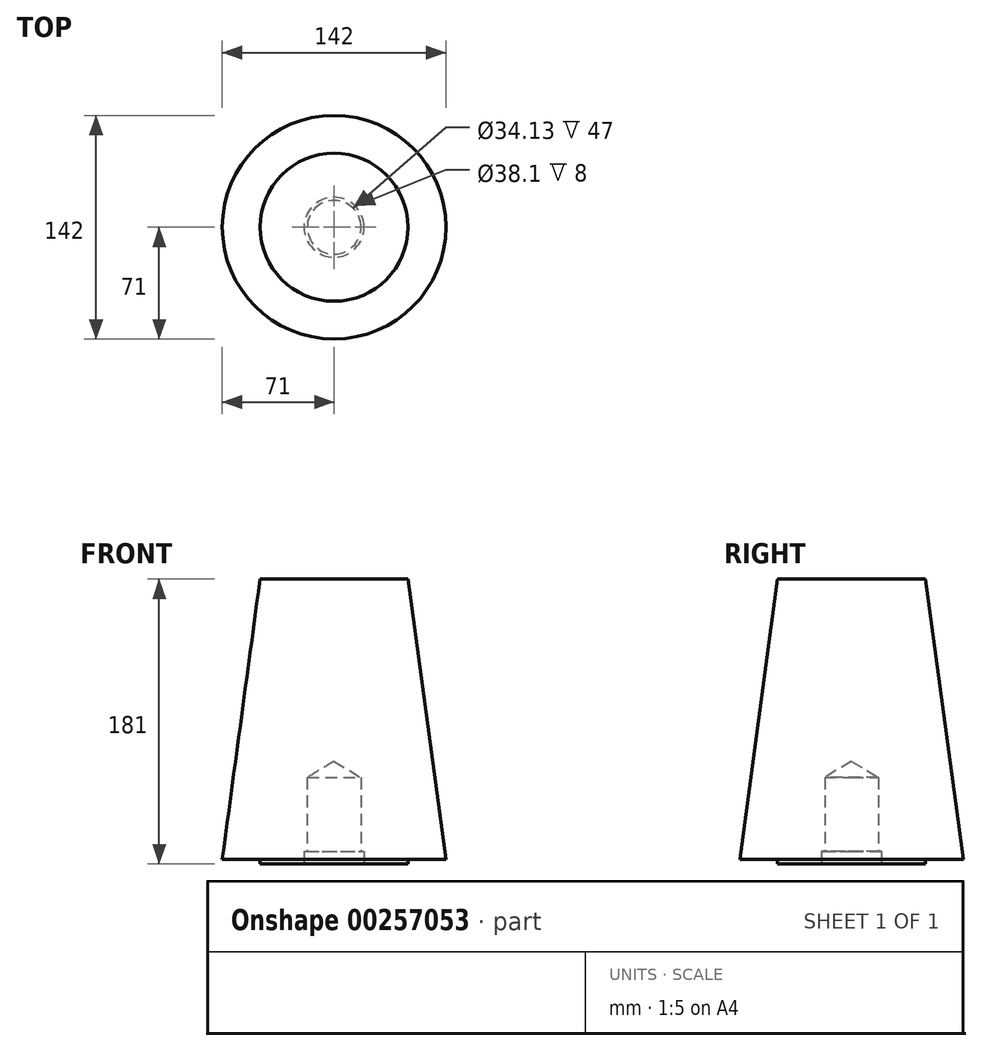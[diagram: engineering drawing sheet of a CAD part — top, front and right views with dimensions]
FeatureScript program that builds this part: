
annotation { "Feature Type Name" : "Feature", "Feature Type Description" : "" }
export const myFeature = defineFeature(function(context is Context, id is Id, definition is map)
    precondition{}
    {
        {
            var Q0;
            Q0=qCreatedBy(makeId("Front.planeOp"),FACE);
            var sketch = newSketch(context, id + "F0", { "sketchPlane" : qUnion([Q0])});
            skLineSegment(sketch, "E0", {"start": v(47, 0) * mm, "end": v(71, 0) * mm});
            skLineSegment(sketch, "E1", {"start": v(0, 0) * mm, "end": v(0, 178) * mm});
            skLineSegment(sketch, "E2", {"start": v(0, 178) * mm, "end": v(47, 178) * mm});
            skLineSegment(sketch, "E3", {"start": v(47, 178) * mm, "end": v(71, 0) * mm});
            skLineSegment(sketch, "E4", {"start": v(0, 0) * mm, "end": v(0, -3) * mm});
            skLineSegment(sketch, "E5", {"start": v(0, -3) * mm, "end": v(47, -3) * mm});
            skLineSegment(sketch, "E6", {"start": v(47, -3) * mm, "end": v(47, 0) * mm});
            skSolve(sketch);
        }
        {
            var Q0;
            Q0 = qSketchRegion(id + "F0", true);
            var Q1;
            Q1=sQuery(id+"F0.wireOp",EDGE,"E1");
            revolve(context, id + "F1", {"entities" : qUnion([Q0]), "axis" : qUnion([Q1]), "revolveType" : RevolveType.FULL});
        }
        {
            var Q0;
            Q0=makeQuery(id+"F1.opRevolve","SWEPT_FACE",FACE,{"disambiguationData":[OSD([sQuery(id+"F0.wireOp",EDGE,"E5")])]});
            var sketch = newSketch(context, id + "F2", { "sketchPlane" : qUnion([Q0])});
            skPoint(sketch, "E7", {"position": v(0, 0) * mm});
            skSolve(sketch);
        }
        {
            var Q0;
            Q0=sQuery(id+"F2.wireOp",VERTEX,"E7");
            var Q1;
            Q1=makeQuery(id+"F1.opRevolve","SWEPT_BODY",BODY,{"disambiguationData":[OSD([sQuery(id+"F0.wireOp",EDGE,"E0"),sQuery(id+"F0.wireOp",EDGE,"E1"),sQuery(id+"F0.wireOp",EDGE,"E2"),sQuery(id+"F0.wireOp",EDGE,"E3"),sQuery(id+"F0.wireOp",EDGE,"E4"),sQuery(id+"F0.wireOp",EDGE,"E5"),sQuery(id+"F0.wireOp",EDGE,"E6")])]});
            hole(context, id + "F3", {"style" : HoleStyle.C_BORE, "endStyle" : HoleEndStyle.BLIND, "holeDiameter" : 34.13 * mm, "cBoreDiameter" : 38.1 * mm, "cBoreDepth" : 8 * mm, "holeDepth" : 55 * mm, "tappedDepth" : 57 * mm, "tapClearance" : 3, "startFromSketch" : true, "locations" : qUnion([Q0]), "scope" : qUnion([Q1])});
        }
    });
